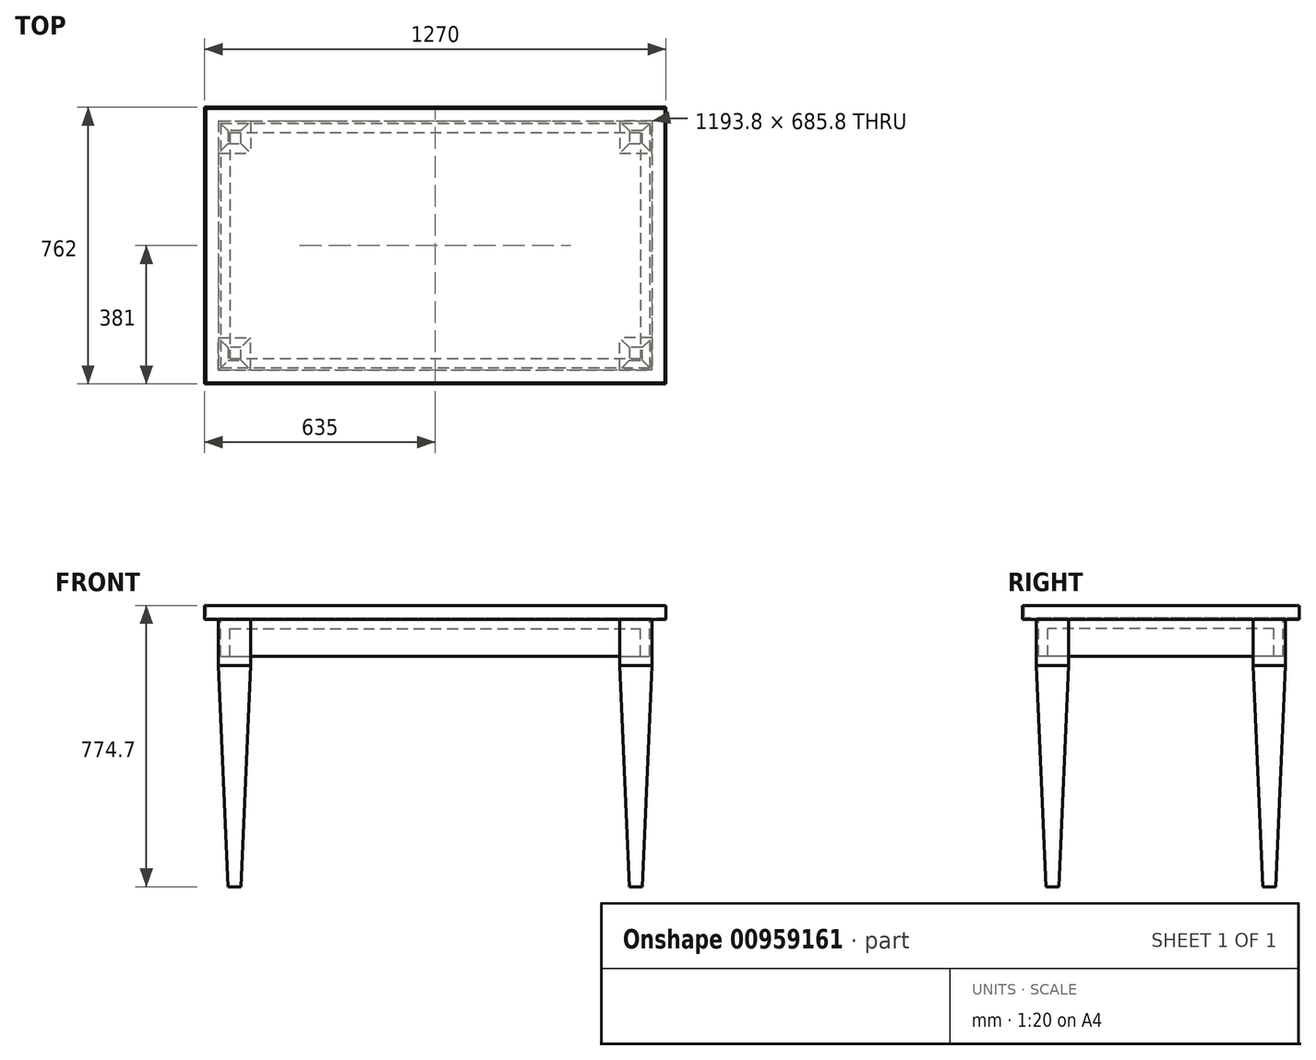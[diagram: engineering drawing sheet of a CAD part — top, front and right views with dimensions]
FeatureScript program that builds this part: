
annotation { "Feature Type Name" : "Feature", "Feature Type Description" : "" }
export const myFeature = defineFeature(function(context is Context, id is Id, definition is map)
    precondition{}
    {
        {
            var Q0;
            Q0=qCreatedBy(makeId("Top.planeOp"),FACE);
            var sketch = newSketch(context, id + "F0", { "sketchPlane" : qUnion([Q0])});
            skLineSegment(sketch, "E0.bottom", {"start": v(-635, 381) * mm, "end": v(635, 381) * mm});
            skLineSegment(sketch, "E0.top", {"start": v(-635, -381) * mm, "end": v(635, -381) * mm});
            skLineSegment(sketch, "E0.left", {"start": v(-635, 381) * mm, "end": v(-635, -381) * mm});
            skLineSegment(sketch, "E0.right", {"start": v(635, 381) * mm, "end": v(635, -381) * mm});
            skPoint(sketch, "E0.middle", {"position": v(0, 0) * mm});
            skLineSegment(sketch, "E1.0", {"start": v(-631.82, 377.83) * mm, "end": v(631.83, 377.83) * mm});
            skLineSegment(sketch, "E1.1", {"start": v(-631.82, 377.83) * mm, "end": v(-631.83, -377.82) * mm});
            skLineSegment(sketch, "E1.2", {"start": v(-631.83, -377.82) * mm, "end": v(631.82, -377.82) * mm});
            skLineSegment(sketch, "E1.3", {"start": v(631.83, 377.83) * mm, "end": v(631.82, -377.82) * mm});
            skLineSegment(sketch, "E2.0", {"start": v(-596.9, 342.9) * mm, "end": v(596.9, 342.9) * mm});
            skLineSegment(sketch, "E2.1", {"start": v(-596.9, 342.9) * mm, "end": v(-596.9, -342.9) * mm});
            skLineSegment(sketch, "E2.2", {"start": v(-596.9, -342.9) * mm, "end": v(596.9, -342.9) * mm});
            skLineSegment(sketch, "E2.3", {"start": v(596.9, 342.9) * mm, "end": v(596.9, -342.9) * mm});
            skSolve(sketch);
        }
        {
            var Q0;
            Q0=qSketchRegion(id+"F0",true);
            extrude(context, id + "F1", {"entities" : qUnion([Q0]), "depth" : 38.1 * mm, "offsetDistance" : 25.4 * mm});
        }
        {
            var Q0;
            Q0=makeQuery(id+"F1.opExtrude","CAP_FACE",FACE,{"disambiguationData":[OSD([sQuery(id+"F0.wireOp",EDGE,"E0.bottom"),sQuery(id+"F0.wireOp",EDGE,"E0.top"),sQuery(id+"F0.wireOp",EDGE,"E0.left"),sQuery(id+"F0.wireOp",EDGE,"E0.right")])],"isStart":true});
            var sketch = newSketch(context, id + "F2", { "sketchPlane" : qUnion([Q0])});
            skLineSegment(sketch, "E3.bottom", {"start": v(-635, -381) * mm, "end": v(635, -381) * mm});
            skLineSegment(sketch, "E3.top", {"start": v(-635, 381) * mm, "end": v(635, 381) * mm});
            skLineSegment(sketch, "E3.left", {"start": v(-635, -381) * mm, "end": v(-635, 381) * mm});
            skLineSegment(sketch, "E3.right", {"start": v(635, -381) * mm, "end": v(635, 381) * mm});
            skPoint(sketch, "E3.middle", {"position": v(0, 0) * mm});
            skLineSegment(sketch, "E4.0", {"start": v(-596.9, -342.9) * mm, "end": v(-596.9, 342.9) * mm});
            skLineSegment(sketch, "E4.1", {"start": v(-596.9, -342.9) * mm, "end": v(596.9, -342.9) * mm});
            skLineSegment(sketch, "E4.2", {"start": v(596.9, -342.9) * mm, "end": v(596.9, 342.9) * mm});
            skLineSegment(sketch, "E4.3", {"start": v(-596.9, 342.9) * mm, "end": v(596.9, 342.9) * mm});
            skLineSegment(sketch, "E5.0", {"start": v(-590.55, 336.55) * mm, "end": v(590.55, 336.55) * mm});
            skLineSegment(sketch, "E5.1", {"start": v(-590.55, -336.55) * mm, "end": v(-590.55, 336.55) * mm});
            skLineSegment(sketch, "E5.2", {"start": v(-590.55, -336.55) * mm, "end": v(590.55, -336.55) * mm});
            skLineSegment(sketch, "E5.3", {"start": v(590.55, -336.55) * mm, "end": v(590.55, 336.55) * mm});
            skLineSegment(sketch, "E6.bottom", {"start": v(-596.9, 342.9) * mm, "end": v(-508, 342.9) * mm});
            skLineSegment(sketch, "E6.top", {"start": v(-596.9, 254) * mm, "end": v(-508, 254) * mm});
            skLineSegment(sketch, "E6.left", {"start": v(-596.9, 342.9) * mm, "end": v(-596.9, 254) * mm});
            skLineSegment(sketch, "E6.right", {"start": v(-508, 342.9) * mm, "end": v(-508, 254) * mm});
            skLineSegment(sketch, "E7", {"start": v(-775.87, 0) * mm, "end": v(783.48, 0) * mm, "construction": true});
            skLineSegment(sketch, "E8", {"start": v(0, 524.15) * mm, "end": v(0, -552.6) * mm, "construction": true});
            skLineSegment(sketch, "E9.MirrorCS", {"start": v(-508, -342.9) * mm, "end": v(-508, -254) * mm});
            skLineSegment(sketch, "E10.MirrorCS", {"start": v(-596.9, -342.9) * mm, "end": v(-508, -342.9) * mm});
            skLineSegment(sketch, "E11.MirrorCS", {"start": v(-596.9, -342.9) * mm, "end": v(-596.9, -254) * mm});
            skLineSegment(sketch, "E12.MirrorCS", {"start": v(-596.9, -254) * mm, "end": v(-508, -254) * mm});
            skSolve(sketch);
        }
        {
            var Q0;
            {var subQ0=sQuery(id+"F2.wireOp",EDGE,"E5.3");Q0=makeQuery(id+"F2.imprint","IMPRINT",FACE,{"disambiguationData":[TD([[makeQuery(id+"F2.imprint","IMPRINT",EDGE,{"derivedFrom":subQ0}),1.0]])]});}
            var sketch = newSketch(context, id + "F3", { "sketchPlane" : qUnion([Q0])});
            skLineSegment(sketch, "E13.0", {"start": v(-596.9, 342.9) * mm, "end": v(-508, 342.9) * mm});
            skLineSegment(sketch, "E14.0", {"start": v(-508, 342.9) * mm, "end": v(-508, 254) * mm});
            skLineSegment(sketch, "E15.0", {"start": v(-596.9, 342.9) * mm, "end": v(-596.9, 254) * mm});
            skLineSegment(sketch, "E16.0", {"start": v(-596.9, 254) * mm, "end": v(-508, 254) * mm});
            skLineSegment(sketch, "E17.0", {"start": v(-596.9, -254) * mm, "end": v(-508, -254) * mm});
            skLineSegment(sketch, "E18.0", {"start": v(-508, -342.9) * mm, "end": v(-508, -254) * mm});
            skLineSegment(sketch, "E19.0", {"start": v(-596.9, -342.9) * mm, "end": v(-508, -342.9) * mm});
            skLineSegment(sketch, "E20.0", {"start": v(-596.9, -342.9) * mm, "end": v(-596.9, -254) * mm});
            skSolve(sketch);
        }
        {
            var Q0;
            Q0=qSketchRegion(id+"F3",true);
            extrude(context, id + "F4", {"entities" : qUnion([Q0]), "depth" : 127 * mm, "offsetDistance" : 25.4 * mm});
        }
        {
            var Q0;
            Q0=makeQuery(id+"F4.opExtrude","SWEPT_BODY",BODY,{"disambiguationData":[OSD([sQuery(id+"F3.wireOp",EDGE,"E13.0"),sQuery(id+"F3.wireOp",EDGE,"E14.0"),sQuery(id+"F3.wireOp",EDGE,"E15.0"),sQuery(id+"F3.wireOp",EDGE,"E16.0")])]});
            var Q1;
            Q1=makeQuery(id+"F4.opExtrude","SWEPT_BODY",BODY,{"disambiguationData":[OSD([sQuery(id+"F3.wireOp",EDGE,"E17.0"),sQuery(id+"F3.wireOp",EDGE,"E18.0"),sQuery(id+"F3.wireOp",EDGE,"E19.0"),sQuery(id+"F3.wireOp",EDGE,"E20.0")])]});
            var Q2;
            Q2=qCreatedBy(makeId("Right.planeOp"),FACE);
            mirror(context, id + "F5", {"operationType" : NewBodyOperationType.ADD, "entities" : qUnion([Q0, Q1]), "mirrorPlane" : qUnion([Q2])});
        }
        {
            var Q0;
            {var subQ0=sQuery(id+"F2.wireOp",EDGE,"E5.3");Q0=makeQuery(id+"F2.imprint","IMPRINT",FACE,{"disambiguationData":[TD([[makeQuery(id+"F2.imprint","IMPRINT",EDGE,{"derivedFrom":subQ0}),1.0]])]});}
            var sketch = newSketch(context, id + "F6", { "sketchPlane" : qUnion([Q0])});
            skLineSegment(sketch, "E21.0", {"start": v(-590.55, 336.55) * mm, "end": v(590.55, 336.55) * mm});
            skLineSegment(sketch, "E22.0", {"start": v(-590.55, -336.55) * mm, "end": v(-590.55, 336.55) * mm});
            skLineSegment(sketch, "E23.0", {"start": v(-590.55, -336.55) * mm, "end": v(590.55, -336.55) * mm});
            skLineSegment(sketch, "E24.0", {"start": v(590.55, -336.55) * mm, "end": v(590.55, 336.55) * mm});
            skSolve(sketch);
        }
        {
            var Q0;
            Q0=qSketchRegion(id+"F6",true);
            extrude(context, id + "F7", {"entities" : qUnion([Q0]), "depth" : 101.6 * mm, "offsetDistance" : 25.4 * mm});
        }
        {
            var Q0;
            Q0=makeQuery(id+"F7.opExtrude","CAP_FACE",FACE,{"disambiguationData":[OSD([sQuery(id+"F6.wireOp",EDGE,"E21.0"),sQuery(id+"F6.wireOp",EDGE,"E22.0"),sQuery(id+"F6.wireOp",EDGE,"E23.0"),sQuery(id+"F6.wireOp",EDGE,"E24.0")])],"isStart":false});
            var Q1;
            Q1=makeQuery(id+"F7.opExtrude","SWEPT_BODY",BODY,{"disambiguationData":[OSD([sQuery(id+"F6.wireOp",EDGE,"E21.0"),sQuery(id+"F6.wireOp",EDGE,"E22.0"),sQuery(id+"F6.wireOp",EDGE,"E23.0"),sQuery(id+"F6.wireOp",EDGE,"E24.0")])]});
            shell(context, id + "F8", {"entities" : qUnion([Q0]), "parts" : qUnion([Q1]), "thickness" : 25.4 * mm});
        }
        {
            var Q0;
            Q0=qCreatedBy(makeId("Top.planeOp"),FACE);
            var sketch = newSketch(context, id + "F9", { "sketchPlane" : qUnion([Q0])});
            skLineSegment(sketch, "E25.0", {"start": v(-596.9, 342.9) * mm, "end": v(596.9, 342.9) * mm});
            skLineSegment(sketch, "E26.0", {"start": v(-596.9, 342.9) * mm, "end": v(-596.9, -342.9) * mm});
            skLineSegment(sketch, "E27.0", {"start": v(-596.9, -342.9) * mm, "end": v(596.9, -342.9) * mm});
            skLineSegment(sketch, "E28.0", {"start": v(596.9, 342.9) * mm, "end": v(596.9, -342.9) * mm});
            skLineSegment(sketch, "E29.0", {"start": v(-635, 381) * mm, "end": v(635, 381) * mm});
            skLineSegment(sketch, "E30.0", {"start": v(-635, 381) * mm, "end": v(-635, -381) * mm});
            skLineSegment(sketch, "E31.0", {"start": v(-635, -381) * mm, "end": v(635, -381) * mm});
            skLineSegment(sketch, "E32.0", {"start": v(635, 381) * mm, "end": v(635, -381) * mm});
            skSolve(sketch);
        }
        {
            var Q0;
            Q0 = qSketchRegion(id + "F9", true);
            extrude(context, id + "F10", {"entities" : qUnion([Q0]), "operationType" : NewBodyOperationType.ADD, "depth" : 3.17 * mm, "offsetDistance" : 25.4 * mm});
        }
        {
            var Q0;
            Q0=qCreatedBy(makeId("Top.planeOp"),FACE);
            var sketch = newSketch(context, id + "F11", { "sketchPlane" : qUnion([Q0])});
            skLineSegment(sketch, "E33.0", {"start": v(-635, 381) * mm, "end": v(635, 381) * mm});
            skLineSegment(sketch, "E34.0", {"start": v(-635, 381) * mm, "end": v(-635, -381) * mm});
            skLineSegment(sketch, "E35.0", {"start": v(-635, -381) * mm, "end": v(635, -381) * mm});
            skLineSegment(sketch, "E36.0", {"start": v(635, 381) * mm, "end": v(635, -381) * mm});
            skSolve(sketch);
        }
        {
            var Q0;
            Q0 = qSketchRegion(id + "F11", true);
            extrude(context, id + "F12", {"entities" : qUnion([Q0]), "depth" : 38.1 * mm, "offsetDistance" : 25.4 * mm});
        }
        {
            var Q0;
            Q0=makeQuery(id+"F4.opExtrude","CAP_FACE",FACE,{"disambiguationData":[OSD([sQuery(id+"F3.wireOp",EDGE,"E13.0"),sQuery(id+"F3.wireOp",EDGE,"E14.0"),sQuery(id+"F3.wireOp",EDGE,"E15.0"),sQuery(id+"F3.wireOp",EDGE,"E16.0")])],"isStart":false});
            var sketch = newSketch(context, id + "F13", { "sketchPlane" : qUnion([Q0])});
            skLineSegment(sketch, "E37.0.0", {"start": v(-596.9, 342.9) * mm, "end": v(-596.9, 254) * mm});
            skLineSegment(sketch, "E37.0.1", {"start": v(-596.9, 254) * mm, "end": v(-508, 254) * mm});
            skLineSegment(sketch, "E37.0.2", {"start": v(-508, 254) * mm, "end": v(-508, 342.9) * mm});
            skLineSegment(sketch, "E37.0.3", {"start": v(-508, 342.9) * mm, "end": v(-596.9, 342.9) * mm});
            skLineSegment(sketch, "E38.0.0", {"start": v(596.9, 254) * mm, "end": v(596.9, 342.9) * mm});
            skLineSegment(sketch, "E38.0.1", {"start": v(596.9, 342.9) * mm, "end": v(508, 342.9) * mm});
            skLineSegment(sketch, "E38.0.2", {"start": v(508, 342.9) * mm, "end": v(508, 254) * mm});
            skLineSegment(sketch, "E38.0.3", {"start": v(508, 254) * mm, "end": v(596.9, 254) * mm});
            skLineSegment(sketch, "E39.0.0", {"start": v(508, -342.9) * mm, "end": v(596.9, -342.9) * mm});
            skLineSegment(sketch, "E39.0.1", {"start": v(596.9, -342.9) * mm, "end": v(596.9, -254) * mm});
            skLineSegment(sketch, "E39.0.2", {"start": v(596.9, -254) * mm, "end": v(508, -254) * mm});
            skLineSegment(sketch, "E39.0.3", {"start": v(508, -254) * mm, "end": v(508, -342.9) * mm});
            skLineSegment(sketch, "E40.0.0", {"start": v(-596.9, -342.9) * mm, "end": v(-508, -342.9) * mm});
            skLineSegment(sketch, "E40.0.1", {"start": v(-508, -342.9) * mm, "end": v(-508, -254) * mm});
            skLineSegment(sketch, "E40.0.2", {"start": v(-508, -254) * mm, "end": v(-596.9, -254) * mm});
            skLineSegment(sketch, "E40.0.3", {"start": v(-596.9, -254) * mm, "end": v(-596.9, -342.9) * mm});
            skSolve(sketch);
        }
        {
            var Q0;
            Q0 = qSketchRegion(id + "F13", true);
            extrude(context, id + "F14", {"entities" : qUnion([Q0]), "depth" : 609.6 * mm, "offsetDistance" : 25.4 * mm, "hasDraft" : true, "draftAngle" : 2.5 * degree, "draftPullDirection" : true});
        }
    });
